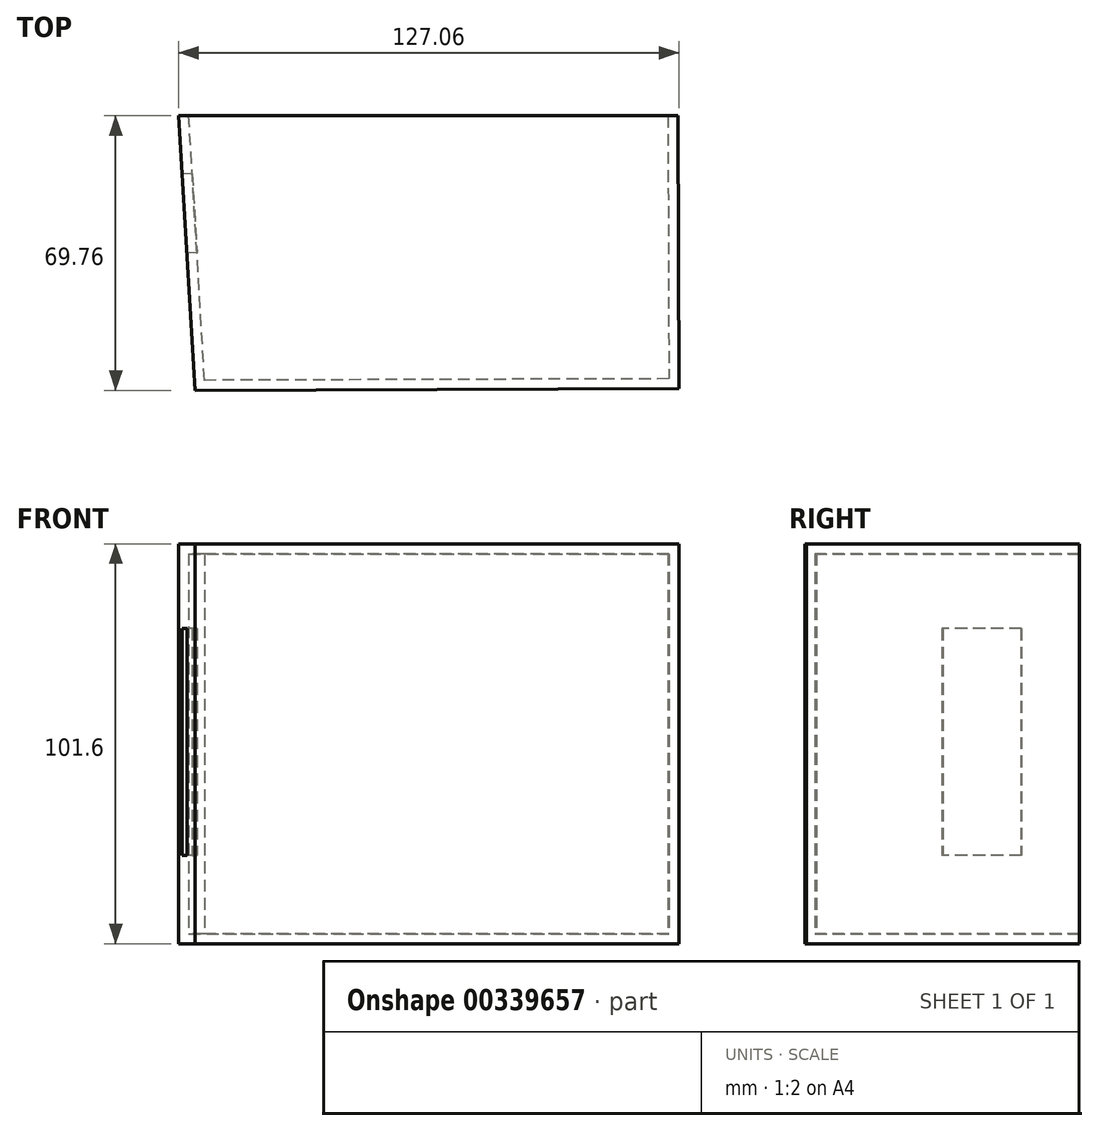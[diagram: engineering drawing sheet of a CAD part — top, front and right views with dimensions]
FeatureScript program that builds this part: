
annotation { "Feature Type Name" : "Feature", "Feature Type Description" : "" }
export const myFeature = defineFeature(function(context is Context, id is Id, definition is map)
    precondition{}
    {
        {
            var Q0;
            Q0=qCreatedBy(makeId("Top.planeOp"),FACE);
            var sketch = newSketch(context, id + "F0", { "sketchPlane" : qUnion([Q0])});
            skLineSegment(sketch, "E0", {"start": v(-94.77, 25.05) * mm, "end": v(32.06, 25.05) * mm});
            skLineSegment(sketch, "E1", {"start": v(32.06, 25.05) * mm, "end": v(32.29, -44.3) * mm});
            skLineSegment(sketch, "E2", {"start": v(32.29, -44.3) * mm, "end": v(-90.62, -44.7) * mm});
            skLineSegment(sketch, "E3", {"start": v(-90.62, -44.7) * mm, "end": v(-94.77, 25.05) * mm});
            skSolve(sketch);
        }
        {
            var Q0;
            Q0=makeQuery(id+"F0.imprint","IMPRINT",FACE,{"disambiguationData":[TD([[makeQuery(id+"F0.imprint","IMPRINT",EDGE,{"derivedFrom":sQuery(id+"F0.wireOp",EDGE,"E0")}),-1.0]])]});
            extrude(context, id + "F1", {"entities" : qUnion([Q0]), "depth" : 101.6 * mm});
        }
        {
            var Q0;
            Q0=makeQuery(id+"F1.opExtrude","SWEPT_FACE",FACE,{"disambiguationData":[OSD([sQuery(id+"F0.wireOp",EDGE,"E0")])]});
            shell(context, id + "F2", {"entities" : qUnion([Q0]), "thickness" : 2.54 * mm});
        }
        {
            var Q0;
            Q0=makeQuery(id+"F1.opExtrude","SWEPT_FACE",FACE,{"disambiguationData":[OSD([sQuery(id+"F0.wireOp",EDGE,"E3")])]});
            var sketch = newSketch(context, id + "F3", { "sketchPlane" : qUnion([Q0])});
            skPoint(sketch, "E4.oppositeSnap0", {"position": v(4.3, 101.6) * mm});
            skLineSegment(sketch, "E4.bottom", {"start": v(-15.77, 80.05) * mm, "end": v(4.3, 80.05) * mm});
            skLineSegment(sketch, "E4.top", {"start": v(-15.77, 22.45) * mm, "end": v(4.3, 22.45) * mm});
            skLineSegment(sketch, "E4.left", {"start": v(-15.77, 80.05) * mm, "end": v(-15.77, 22.45) * mm});
            skLineSegment(sketch, "E4.right", {"start": v(4.3, 80.05) * mm, "end": v(4.3, 22.45) * mm});
            skSolve(sketch);
        }
        {
            var Q0;
            Q0 = qSketchRegion(id + "F3", true);
            extrude(context, id + "F4", {"entities" : qUnion([Q0]), "operationType" : NewBodyOperationType.REMOVE, "oppositeDirection" : true, "depth" : 50.8 * mm});
        }
    });
